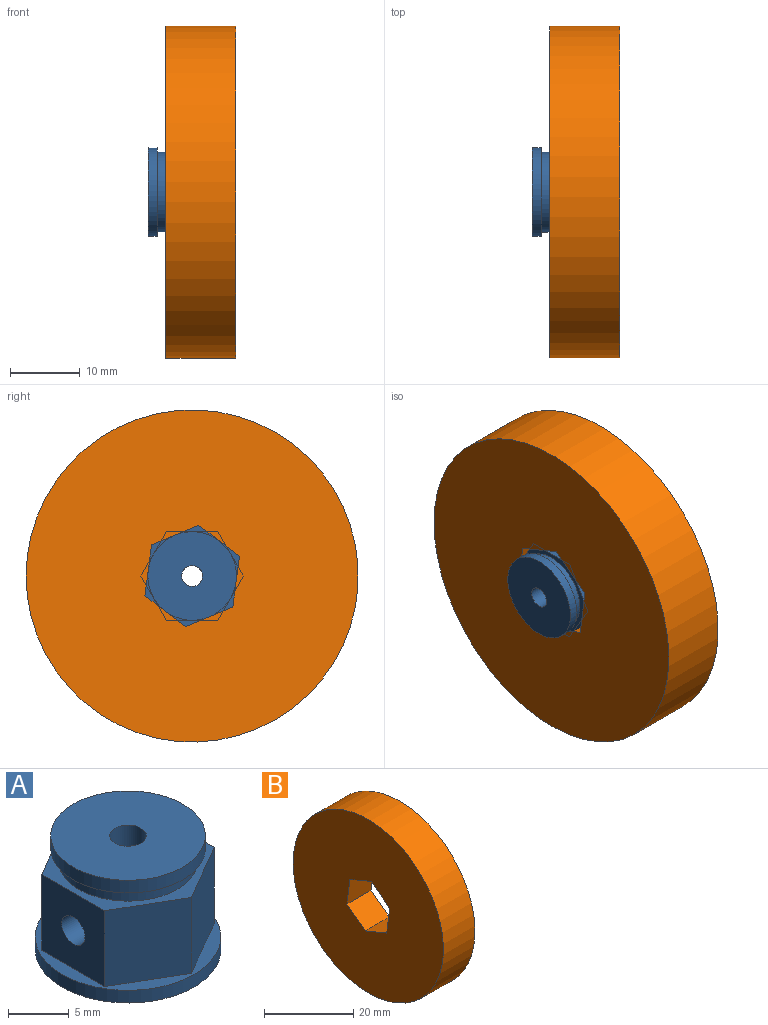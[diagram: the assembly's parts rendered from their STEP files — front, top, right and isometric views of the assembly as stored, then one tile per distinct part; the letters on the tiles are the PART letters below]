
ASSEMBLY  parts=2 mates=1
PART A: 16 faces, bbox 15.2x15.2x11.4 mm
  f0: cylinder r=1.5mm len=11.43mm, axis (0,0,1), area 101mm2, adj f3,f13,f15
  f1: plane 15.24x15.24mm, normal (0,0,1), area 42.7mm2, adj f2,f4,f5,f6,f7,f8,f9
  f2: cylinder r=7.62mm len=15.24mm, axis (0,0,-1), area 60.8mm2, adj f1,f3
  f3: plane 15.24x15.24mm, normal (0,0,-1), area 175.3mm2, adj f0,f2
  f4: plane 7.62x7.33mm, normal (1,0,0), area 55.9mm2, adj f1,f5,f9,f10
  f5: plane 7.62x6.35mm, normal (0.5,0.87,0), area 55.9mm2, adj f1,f4,f6,f10
  f6: plane 7.62x6.35mm, normal (-0.5,0.87,0), area 55.9mm2, adj f1,f5,f7,f10
  f7: plane 7.62x7.33mm, normal (-1,0,0), area 50.1mm2, adj f1,f6,f8,f10,f15
  f8: plane 7.62x6.35mm, normal (-0.5,-0.87,0), area 55.9mm2, adj f1,f7,f9,f10
  f9: plane 7.62x6.35mm, normal (0.5,-0.87,0), area 55.9mm2, adj f1,f4,f8,f10
  f10: plane 14.66x12.7mm, normal (0,0,1), area 37.1mm2, adj f4,f5,f6,f7,f8,f9,f11
  f11: cylinder r=5.71mm len=11.43mm, axis (0,0,-1), area 45.6mm2, adj f10,f14
  f12: cylinder r=6.35mm len=12.7mm, axis (0,0,-1), area 50.7mm2, adj f13,f14
  f13: plane 12.7x12.7mm, normal (0,0,1), area 119.6mm2, adj f0,f12
  f14: plane 12.7x12.7mm, normal (0,0,-1), area 24.1mm2, adj f11,f12
  f15: cylinder r=1.35mm len=5.7mm, axis (-1,0,0), area 44.5mm2, adj f0,f7
PART B: 11 faces, bbox 10x47.6x47.6 mm
  f0: cylinder r=23.8mm len=47.6mm, axis (-1,0,0), area 1495.4mm2, adj f1,f2
  f1: plane 47.6x47.6mm, normal (1,0,0), area 669.2mm2, adj f0,f3
  f2: plane 47.6x47.6mm, normal (-1,0,0), area 1639.8mm2, adj f0,f5,f6,f7,f8,f9,f10
  f3: cylinder r=18.8mm len=37.6mm, axis (1,0,0), area 283.5mm2, adj f1,f4
  f4: plane 37.6x37.6mm, normal (1,0,0), area 970.7mm2, adj f3,f5,f6,f7,f8,f9,f10
  f5: plane 7.6x6.77mm, normal (0,0.38,0.92), area 55.7mm2, adj f2,f4,f6,f10
  f6: plane 7.6x5.82mm, normal (0,-0.61,0.79), area 55.7mm2, adj f2,f4,f5,f7
  f7: plane 7.6x7.27mm, normal (0,-0.99,-0.13), area 55.7mm2, adj f2,f4,f6,f8
  f8: plane 7.6x6.77mm, normal (0,-0.38,-0.92), area 55.7mm2, adj f2,f4,f7,f9
  f9: plane 7.6x5.82mm, normal (0,0.61,-0.79), area 55.7mm2, adj f2,f4,f8,f10
  f10: plane 7.6x7.27mm, normal (0,0.99,0.13), area 55.7mm2, adj f2,f4,f5,f9
PLACE A rot(axis=(0.71,0,-0.71),180deg) t=(17.58,9.37,2.24)mm
PLACE B t=(8.65,9.37,2.24)mm
MATE fastened A.f0 <-> B.f0  axis (-1,0,0) through (6.15,9.37,2.24)mm
